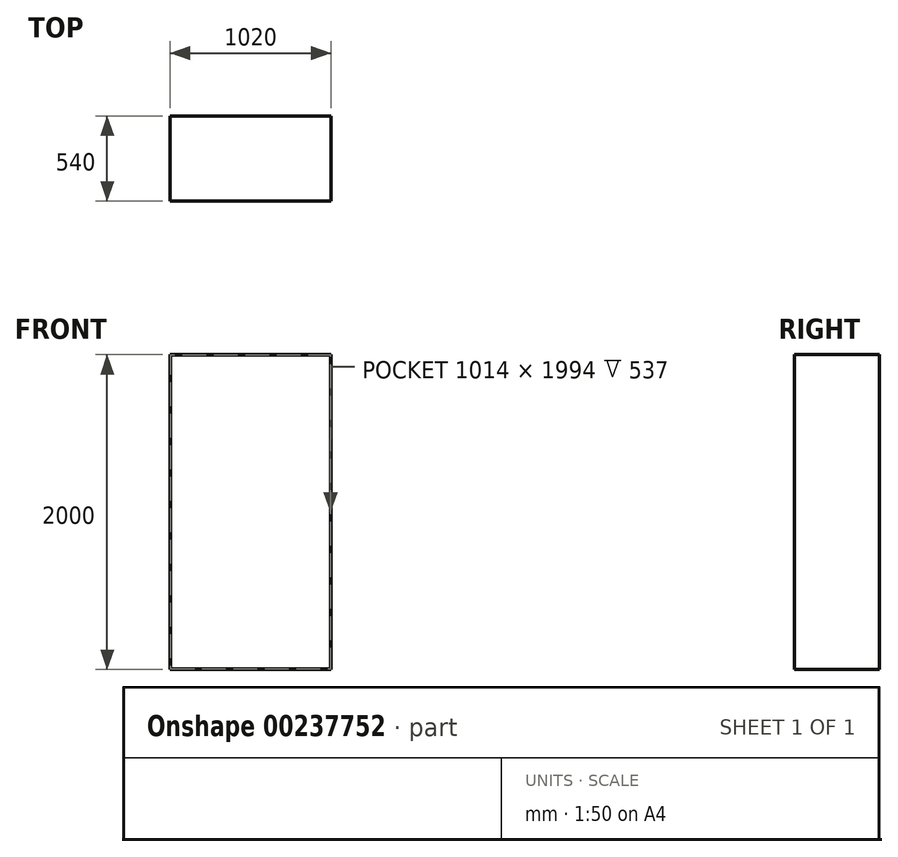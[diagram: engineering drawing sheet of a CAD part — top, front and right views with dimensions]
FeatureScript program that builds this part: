
annotation { "Feature Type Name" : "Feature", "Feature Type Description" : "" }
export const myFeature = defineFeature(function(context is Context, id is Id, definition is map)
    precondition{}
    {
        {
            var Q0;
            Q0=qCreatedBy(makeId("Top.planeOp"),FACE);
            var sketch = newSketch(context, id + "F0", { "sketchPlane" : qUnion([Q0])});
            skLineSegment(sketch, "E0.bottom", {"start": v(0, 0) * mm, "end": v(-1020, 0) * mm});
            skLineSegment(sketch, "E0.top", {"start": v(0, 540) * mm, "end": v(-1020, 540) * mm});
            skLineSegment(sketch, "E0.left", {"start": v(0, 0) * mm, "end": v(0, 540) * mm});
            skLineSegment(sketch, "E0.right", {"start": v(-1020, 0) * mm, "end": v(-1020, 540) * mm});
            skSolve(sketch);
        }
        {
            var Q0;
            Q0=makeQuery(id+"F0.imprint","IMPRINT",FACE,{"disambiguationData":[TD([[makeQuery(id+"F0.imprint","IMPRINT",EDGE,{"derivedFrom":sQuery(id+"F0.wireOp",EDGE,"E0.bottom")}),-1.0]])]});
            extrude(context, id + "F1", {"entities" : qUnion([Q0]), "depth" : 2000 * mm});
        }
        {
            var Q0;
            Q0=makeQuery(id+"F1.opExtrude","SWEPT_FACE",FACE,{"disambiguationData":[OSD([sQuery(id+"F0.wireOp",EDGE,"E0.bottom")])]});
            shell(context, id + "F2", {"entities" : qUnion([Q0]), "thickness" : 3 * mm});
        }
    });
